# Revit family: FU_Inspec_Grade_1-2
name_source: partatom
category: Furniture
units: mm (PartAtom-declared; Revit-internal decimal feet)

## family parameters
Always vertical = Yes
Cut with Voids When Loaded = No
OmniClass Number = 23.40.20.00
OmniClass Title = General Furniture and Specialties
Room Calculation Point = No
Shared = No
Work Plane-Based = No

## types (6) — shared parameters
Assembly Code = E2020
Depth = 540 mm  [stored 1.77165 ft]
Height = 780 mm  [stored 2.55906 ft]
Keynote = 46.B
Manufacturer = Inspec
URL = https://inspecfurniture.com
Weight = 4.5
Width = 510 mm  [stored 1.67323 ft]
zero-valued in all types: Default Elevation

## per-type parameters (varying)
| type | Description | Frame Material | Model | Seat Material | Seat Pad Material |
| Grade 1.1 - Chrome - White | Chair with recycled polypropylene seat on a powder coated or chromium plated tubular steel frame. Stackable and linkable | Metal - Chrome - Polished | Grade 1.1 | Colour - Coated - White | Fabric - Divina 3 - 236 |
| Grade 1.1 - Coated - Black | Chair with recycled polypropylene seat on a powder coated or chromium plated tubular steel frame. Stackable and linkable | Colour - Coated - Black | Grade 1.1 | Colour - Coated - Black | Fabric - Divina 3 - 691 |
| Grade 1.2 - Chrome - Green | Chair with recycled polypropylene seat on a powder coated or chromium plated tubular steel frame. With upholstered seat pad. Stackable and linkable | Metal - Chrome - Polished | Grade 1.2 | Colour - Coated - Blue green | Fabric - Divina 3 - 236 |
| Grade 1.2 - Coated - Red | Chair with recycled polypropylene seat on a powder coated or chromium plated tubular steel frame. With upholstered seat pad. Stackable and linkable | Colour - Coated - Black | Grade 1.2 | Colour - Coated - Dark red | Fabric - Divina Red |
| Grade 1.3 - Coated - Red | Chair with fully upholstered recycled polypropylene seat on a powder coated or chromium plated tubular steel frame. Stackable and linkable | Colour - Coated - Dark red | Grade 1.3 | Colour - Coated - Dark red | Fabric - Divina Red |
| Grade 1.3 - Black - Black | Chair with fully upholstered recycled polypropylene seat on a powder coated or chromium plated tubular steel frame. Stackable and linkable | Colour - Coated - Black | Grade 1.3 | Fabric - Divina Black | Fabric - Divina Black |

note: [stored X ft] marks values corroborated as IEEE doubles in the binary element streams (Revit-internal decimal feet)

## geometry (parser evidence)
native form markers: Blend x416, Sweep x1
no freeform markers — native parametric forms only
